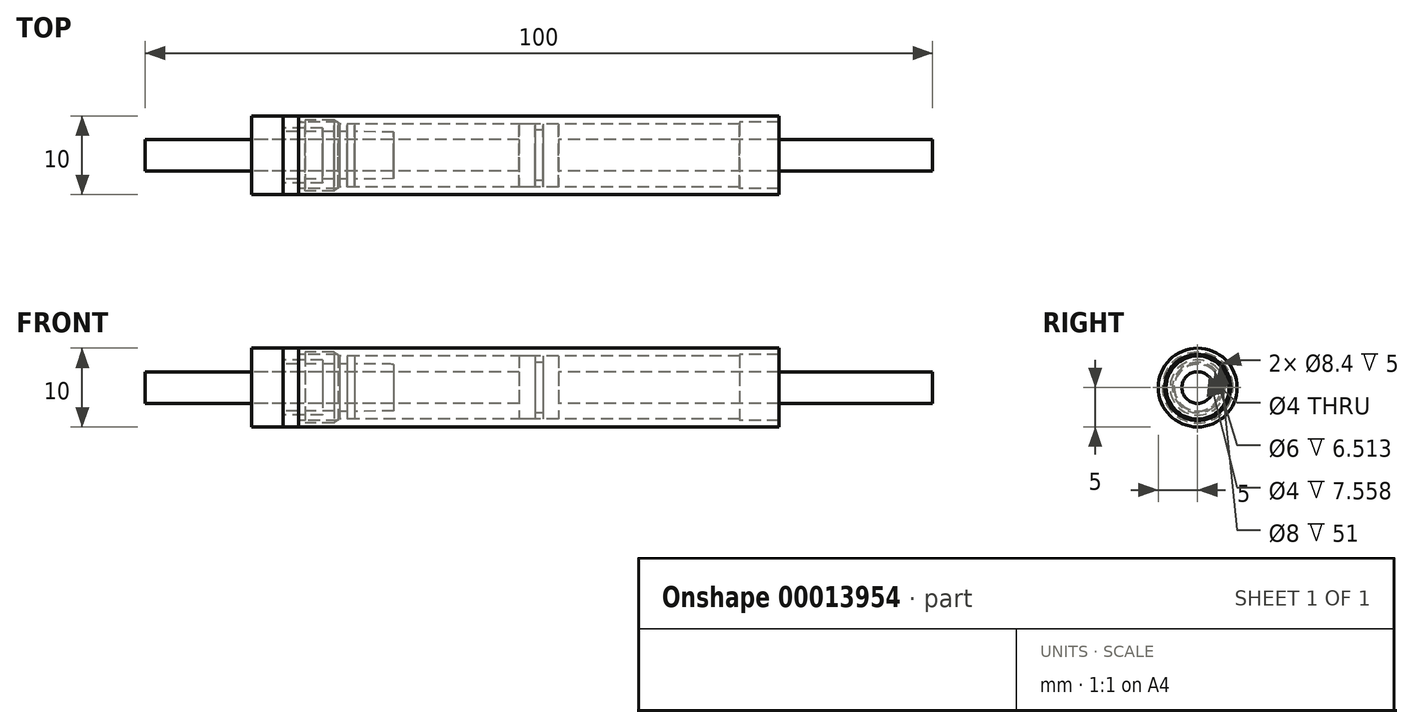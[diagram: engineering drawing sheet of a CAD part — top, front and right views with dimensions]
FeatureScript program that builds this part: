
annotation { "Feature Type Name" : "Feature", "Feature Type Description" : "" }
export const myFeature = defineFeature(function(context is Context, id is Id, definition is map)
    precondition{}
    {
        {
            var Q0;
            Q0=qCreatedBy(makeId("Front.planeOp"),FACE);
            var sketch = newSketch(context, id + "F0", { "sketchPlane" : qUnion([Q0])});
            skLineSegment(sketch, "E0", {"start": v(-70.46, 0) * mm, "end": v(66.88, 0) * mm, "construction": true});
            skLineSegment(sketch, "E1.bottom", {"start": v(-30.5, 5) * mm, "end": v(30.5, 5) * mm});
            skLineSegment(sketch, "E1.top", {"start": v(-25.5, 4) * mm, "end": v(25.5, 4) * mm});
            skLineSegment(sketch, "E1.left", {"start": v(-30.5, 5) * mm, "end": v(-30.5, 4.2) * mm});
            skLineSegment(sketch, "E1.right", {"start": v(30.5, 5) * mm, "end": v(30.5, 4.2) * mm});
            skPoint(sketch, "E2", {"position": v(0, 5) * mm});
            skLineSegment(sketch, "E3", {"start": v(-30.5, 4.2) * mm, "end": v(-25.5, 4.2) * mm});
            skLineSegment(sketch, "E4", {"start": v(-25.5, 4.2) * mm, "end": v(-25.5, 4) * mm});
            skLineSegment(sketch, "E5", {"start": v(30.5, 4.2) * mm, "end": v(25.5, 4.2) * mm});
            skLineSegment(sketch, "E6", {"start": v(25.5, 4.2) * mm, "end": v(25.5, 4) * mm});
            skSolve(sketch);
        }
        {
            var Q0;
            Q0=makeQuery(id+"F0.imprint","IMPRINT",FACE,{"disambiguationData":[TD([[makeQuery(id+"F0.imprint","IMPRINT",EDGE,{"derivedFrom":sQuery(id+"F0.wireOp",EDGE,"E1.bottom")}),-1.0]])]});
            var Q1;
            Q1=sQuery(id+"F0.wireOp",EDGE,"E0");
            revolve(context, id + "F1", {"entities" : qUnion([Q0]), "axis" : qUnion([Q1]), "revolveType" : RevolveType.FULL});
        }
        {
            var Q0;
            Q0=qCreatedBy(makeId("Front.planeOp"),FACE);
            var sketch = newSketch(context, id + "F2", { "sketchPlane" : qUnion([Q0])});
            skLineSegment(sketch, "E7", {"start": v(-30.5, 5) * mm, "end": v(-32.5, 5) * mm});
            skLineSegment(sketch, "E8", {"start": v(-32.5, 5) * mm, "end": v(-32.5, 3) * mm});
            skLineSegment(sketch, "E9", {"start": v(-25.29, 3.95) * mm, "end": v(-26.03, 4.5) * mm});
            skLineSegment(sketch, "E10", {"start": v(-26.03, 4.5) * mm, "end": v(-29.7, 4.5) * mm});
            skLineSegment(sketch, "E11", {"start": v(-29.7, 4.5) * mm, "end": v(-29.7, 4.19) * mm});
            skLineSegment(sketch, "E12", {"start": v(-29.7, 4.19) * mm, "end": v(-30.5, 4.19) * mm});
            skLineSegment(sketch, "E13", {"start": v(-30.5, 4.19) * mm, "end": v(-30.5, 5) * mm});
            skLineSegment(sketch, "E14", {"start": v(-32.5, 3) * mm, "end": v(-25.99, 3) * mm});
            skLineSegment(sketch, "E15", {"start": v(-25.99, 3) * mm, "end": v(-25.99, 2) * mm});
            skLineSegment(sketch, "E16", {"start": v(-25.99, 2) * mm, "end": v(-18.43, 2) * mm});
            skLineSegment(sketch, "E17", {"start": v(-36.6, 0) * mm, "end": v(-20.19, 0) * mm, "construction": true});
            skLineSegment(sketch, "E18", {"start": v(-25.29, 3.95) * mm, "end": v(-25.29, 3) * mm});
            skLineSegment(sketch, "E19", {"start": v(-25.29, 3) * mm, "end": v(-24.36, 3) * mm});
            skLineSegment(sketch, "E20", {"start": v(-24.36, 3) * mm, "end": v(-24.36, 4) * mm});
            skLineSegment(sketch, "E21", {"start": v(-24.36, 4) * mm, "end": v(-23.43, 4) * mm});
            skLineSegment(sketch, "E22", {"start": v(-18.43, 2.96) * mm, "end": v(-18.43, 2) * mm});
            skLineSegment(sketch, "E23", {"start": v(-23.43, 4) * mm, "end": v(-23.43, 3.02) * mm});
            skLineSegment(sketch, "E24", {"start": v(-23.43, 3.02) * mm, "end": v(-18.43, 2.96) * mm});
            skSolve(sketch);
        }
        {
            var Q0;
            Q0=makeQuery(id+"F2.imprint","IMPRINT",FACE,{"disambiguationData":[TD([[makeQuery(id+"F2.imprint","IMPRINT",EDGE,{"derivedFrom":sQuery(id+"F2.wireOp",EDGE,"E7")}),1.0]])]});
            var Q1;
            Q1=sQuery(id+"F2.wireOp",EDGE,"E17");
            revolve(context, id + "F3", {"entities" : qUnion([Q0]), "axis" : qUnion([Q1]), "revolveType" : RevolveType.FULL});
        }
        {
            var Q0;
            Q0=qCreatedBy(makeId("Front.planeOp"),FACE);
            var sketch = newSketch(context, id + "F4", { "sketchPlane" : qUnion([Q0])});
            skLineSegment(sketch, "E25", {"start": v(-32.5, 5) * mm, "end": v(-36.5, 5) * mm});
            skLineSegment(sketch, "E26", {"start": v(-36.5, 5) * mm, "end": v(-36.5, 2) * mm});
            skLineSegment(sketch, "E27", {"start": v(-36.5, 2) * mm, "end": v(-27.5, 2) * mm});
            skLineSegment(sketch, "E28", {"start": v(-27.5, 2) * mm, "end": v(-27.5, 3.5) * mm});
            skLineSegment(sketch, "E29", {"start": v(-27.5, 3.5) * mm, "end": v(-32.5, 3.5) * mm});
            skLineSegment(sketch, "E30", {"start": v(-32.5, 3.5) * mm, "end": v(-32.5, 5) * mm});
            skSolve(sketch);
        }
        {
            var Q0;
            Q0=makeQuery(id+"F4.imprint","IMPRINT",FACE,{"disambiguationData":[TD([[makeQuery(id+"F4.imprint","IMPRINT",EDGE,{"derivedFrom":sQuery(id+"F4.wireOp",EDGE,"E25")}),1.0]])]});
            var Q1;
            Q1=sQuery(id+"F2.wireOp",EDGE,"E17");
            revolve(context, id + "F5", {"entities" : qUnion([Q0]), "axis" : qUnion([Q1]), "revolveType" : RevolveType.FULL});
        }
        {
            var Q0;
            Q0=qCreatedBy(makeId("Front.planeOp"),FACE);
            var sketch = newSketch(context, id + "F6", { "sketchPlane" : qUnion([Q0])});
            skLineSegment(sketch, "E31", {"start": v(-0.5, 4) * mm, "end": v(-2.5, 4) * mm});
            skLineSegment(sketch, "E32", {"start": v(-2.5, 4) * mm, "end": v(-2.5, 2) * mm});
            skLineSegment(sketch, "E33", {"start": v(-2.5, 2) * mm, "end": v(-50, 2) * mm});
            skLineSegment(sketch, "E34", {"start": v(-50, 2) * mm, "end": v(-50, 0) * mm});
            skLineSegment(sketch, "E35", {"start": v(-50, 0) * mm, "end": v(0, 0) * mm});
            skLineSegment(sketch, "E36.MirrorCS", {"start": v(0.5, 4) * mm, "end": v(2.5, 4) * mm});
            skLineSegment(sketch, "E37.MirrorCS", {"start": v(2.5, 4) * mm, "end": v(2.5, 2) * mm});
            skLineSegment(sketch, "E38.MirrorCS", {"start": v(50, 0) * mm, "end": v(0, 0) * mm});
            skLineSegment(sketch, "E39.MirrorCS", {"start": v(2.5, 2) * mm, "end": v(50, 2) * mm});
            skLineSegment(sketch, "E40.MirrorCS", {"start": v(50, 2) * mm, "end": v(50, 0) * mm});
            skLineSegment(sketch, "E41", {"start": v(-0.5, 4) * mm, "end": v(-0.5, 3.2) * mm});
            skLineSegment(sketch, "E42", {"start": v(-0.5, 3.2) * mm, "end": v(0.5, 3.2) * mm});
            skLineSegment(sketch, "E43", {"start": v(0.5, 3.2) * mm, "end": v(0.5, 4) * mm});
            skPoint(sketch, "E44", {"position": v(0, 3.2) * mm});
            skPoint(sketch, "E45.orphan", {"position": v(0, 4) * mm});
            skSolve(sketch);
        }
        {
            var Q0;
            Q0=makeQuery(id+"F6.imprint","IMPRINT",FACE,{"disambiguationData":[TD([[makeQuery(id+"F6.imprint","IMPRINT",EDGE,{"derivedFrom":sQuery(id+"F6.wireOp",EDGE,"E31")}),1.0]])]});
            var Q1;
            Q1=sQuery(id+"F0.wireOp",EDGE,"E0");
            revolve(context, id + "F7", {"entities" : qUnion([Q0]), "axis" : qUnion([Q1]), "revolveType" : RevolveType.FULL});
        }
    });
